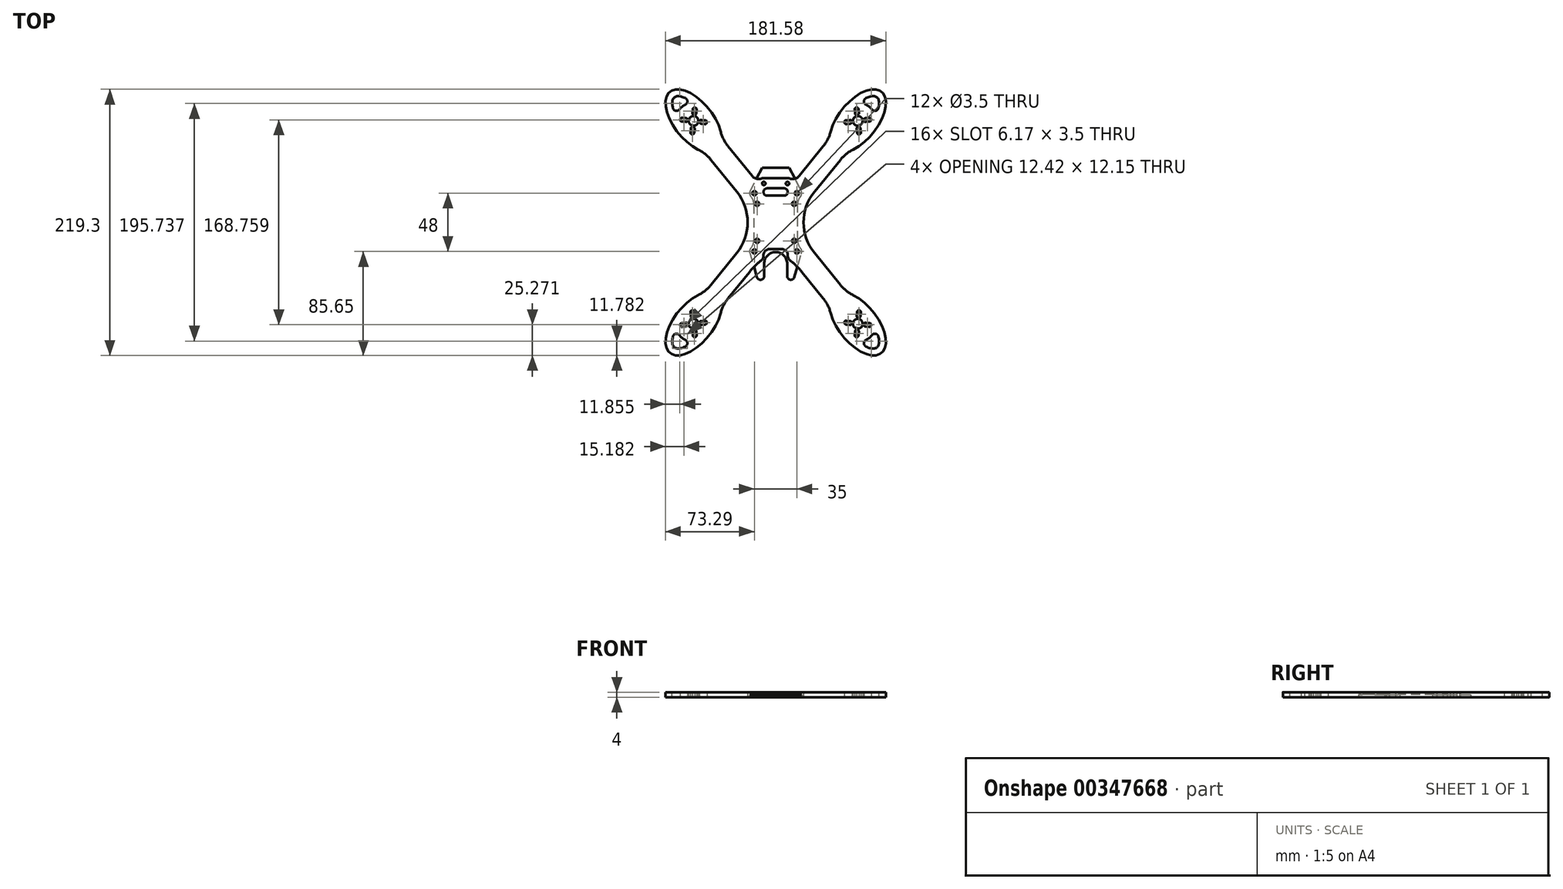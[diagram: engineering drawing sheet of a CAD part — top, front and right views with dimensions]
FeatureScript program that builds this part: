
annotation { "Feature Type Name" : "Feature", "Feature Type Description" : "" }
export const myFeature = defineFeature(function(context is Context, id is Id, definition is map)
    precondition{}
    {
        {
            var Q0;
            Q0=qCreatedBy(makeId("Top.planeOp"),FACE);
            var sketch = newSketch(context, id + "F0", { "sketchPlane" : qUnion([Q0])});
            skCircle(sketch, "E0", {"center": v(0, 0) * mm, "radius": 107.5 * mm, "construction": true});
            skCircle(sketch, "E1", {"center": v(-67.65, 83.54) * mm, "radius": 63.5 * mm, "construction": true});
            skLineSegment(sketch, "E2", {"start": v(-67.65, 83.54) * mm, "end": v(0, 0) * mm, "construction": true});
            skCircle(sketch, "E3", {"center": v(-67.65, 83.54) * mm, "radius": 4 * mm});
            skEllipticalArc(sketch, "E4", {});
            skLineSegment(sketch, "E5", {"start": v(-87.16, 107.63) * mm, "end": v(-67.65, 83.54) * mm, "construction": true});
            skLineSegment(sketch, "E6", {"start": v(-80.09, 73.47) * mm, "end": v(-55.22, 93.61) * mm, "construction": true});
            skLineSegment(sketch, "E7", {"start": v(-53.23, 51.43) * mm, "end": v(-31.97, 25.17) * mm});
            skLineSegment(sketch, "E8", {"start": v(-39.24, 62.76) * mm, "end": v(-21.56, 40.92) * mm});
            skLineSegment(sketch, "E9", {"start": v(-67.65, 83.54) * mm, "end": v(-66.97, 90) * mm, "construction": true});
            skLineSegment(sketch, "E10", {"start": v(-66.97, 90) * mm, "end": v(-66.66, 93) * mm, "construction": true});
            skArc(sketch, "E11.0.startCap", {"start": v(-65.38, 89.84) * mm, "mid": v(-67.14, 88.42) * mm, "end": v(-68.56, 90.17) * mm});
            skArc(sketch, "E11.0.endCap", {"start": v(-68.25, 93.16) * mm, "mid": v(-66.5, 94.58) * mm, "end": v(-65.07, 92.82) * mm});
            skLineSegment(sketch, "E11.0.left", {"start": v(-68.56, 90.17) * mm, "end": v(-68.25, 93.16) * mm});
            skLineSegment(sketch, "E11.0.right", {"start": v(-65.38, 89.84) * mm, "end": v(-65.07, 92.82) * mm});
            skArc(sketch, "E12.1.0", {"start": v(-77.27, 82.94) * mm, "mid": v(-78.7, 84.7) * mm, "end": v(-76.93, 86.13) * mm});
            skLineSegment(sketch, "E12.1.1", {"start": v(-74.28, 82.63) * mm, "end": v(-77.27, 82.94) * mm});
            skArc(sketch, "E12.1.2", {"start": v(-73.95, 85.81) * mm, "mid": v(-72.53, 84.06) * mm, "end": v(-74.28, 82.63) * mm});
            skLineSegment(sketch, "E12.1.3", {"start": v(-73.95, 85.81) * mm, "end": v(-76.93, 86.13) * mm});
            skArc(sketch, "E12.2.0", {"start": v(-67.05, 73.93) * mm, "mid": v(-68.81, 72.5) * mm, "end": v(-70.24, 74.26) * mm});
            skLineSegment(sketch, "E12.2.1", {"start": v(-66.74, 76.91) * mm, "end": v(-67.05, 73.93) * mm});
            skArc(sketch, "E12.2.2", {"start": v(-69.92, 77.25) * mm, "mid": v(-68.16, 78.67) * mm, "end": v(-66.74, 76.91) * mm});
            skLineSegment(sketch, "E12.2.3", {"start": v(-69.92, 77.25) * mm, "end": v(-70.24, 74.26) * mm});
            skArc(sketch, "E12.3.0", {"start": v(-58.04, 84.14) * mm, "mid": v(-56.61, 82.38) * mm, "end": v(-58.37, 80.96) * mm});
            skLineSegment(sketch, "E12.3.1", {"start": v(-61.02, 84.45) * mm, "end": v(-58.04, 84.14) * mm});
            skArc(sketch, "E12.3.2", {"start": v(-61.35, 81.27) * mm, "mid": v(-62.78, 83.03) * mm, "end": v(-61.02, 84.45) * mm});
            skLineSegment(sketch, "E12.3.3", {"start": v(-61.35, 81.27) * mm, "end": v(-58.37, 80.96) * mm});
            skEllipticalArc(sketch, "E13", {});
            skLineSegment(sketch, "E14", {"start": v(-83.38, 102.97) * mm, "end": v(-67.65, 83.54) * mm, "construction": true});
            skArc(sketch, "E15", {"start": v(-79.37, 92.91) * mm, "mid": v(-77.1, 95.2) * mm, "end": v(-74.38, 96.95) * mm});
            skPoint(sketch, "E16.orphan", {"position": v(-81.22, 85.81) * mm});
            skPoint(sketch, "E17.orphan", {"position": v(-67.05, 97.28) * mm});
            skPoint(sketch, "E18.visualSharp", {"position": v(-82.11, 87.53) * mm});
            skArc(sketch, "E18.filletArc", {"start": v(-84.61, 94.04) * mm, "mid": v(-82.34, 91.85) * mm, "end": v(-79.37, 92.91) * mm});
            skPoint(sketch, "E19.visualSharp", {"position": v(-68.55, 98.52) * mm});
            skArc(sketch, "E19.filletArc", {"start": v(-74.38, 96.95) * mm, "mid": v(-72.73, 99.64) * mm, "end": v(-74.4, 102.32) * mm});
            skPoint(sketch, "E20.visualSharp", {"position": v(-58.52, 57.96) * mm});
            skArc(sketch, "E20.filletArc", {"start": v(-53.23, 51.43) * mm, "mid": v(-58.12, 56.29) * mm, "end": v(-63.94, 59.99) * mm});
            skPoint(sketch, "E21.visualSharp", {"position": v(-44.53, 69.29) * mm});
            skArc(sketch, "E21.filletArc", {"start": v(-45.38, 75.01) * mm, "mid": v(-42.98, 68.55) * mm, "end": v(-39.24, 62.76) * mm});
            skArc(sketch, "E22", {"start": v(-23.05, 0) * mm, "mid": v(-25.35, 13.35) * mm, "end": v(-31.97, 25.17) * mm});
            skPoint(sketch, "E23.orphan", {"position": v(0, 14.3) * mm});
            skCircle(sketch, "E24", {"center": v(-15.25, 15.25) * mm, "radius": 1.75 * mm});
            skCircle(sketch, "E25", {"center": v(-17.5, 24) * mm, "radius": 1.75 * mm});
            skLineSegment(sketch, "E26", {"start": v(-23.05, 0) * mm, "end": v(0, 0) * mm, "construction": true});
            skCircle(sketch, "E27.MirrorC", {"center": v(17.5, 24) * mm, "radius": 1.75 * mm});
            skCircle(sketch, "E28.MirrorC", {"center": v(15.25, 15.25) * mm, "radius": 1.75 * mm});
            skArc(sketch, "E29.MirrorCS", {"start": v(23.05, 0) * mm, "mid": v(25.35, 13.35) * mm, "end": v(31.97, 25.17) * mm});
            skLineSegment(sketch, "E30.MirrorCS", {"start": v(53.23, 51.43) * mm, "end": v(31.97, 25.17) * mm});
            skLineSegment(sketch, "E31.MirrorCS", {"start": v(39.24, 62.76) * mm, "end": v(21.56, 40.92) * mm});
            skArc(sketch, "E32.MirrorCS", {"start": v(53.23, 51.43) * mm, "mid": v(58.12, 56.29) * mm, "end": v(63.94, 59.99) * mm});
            skArc(sketch, "E33.MirrorCS", {"start": v(45.38, 75.01) * mm, "mid": v(42.98, 68.55) * mm, "end": v(39.24, 62.76) * mm});
            skEllipticalArc(sketch, "E34.MirrorCS", {});
            skEllipticalArc(sketch, "E35.MirrorCS", {});
            skArc(sketch, "E36.MirrorCS", {"start": v(74.38, 96.95) * mm, "mid": v(72.73, 99.64) * mm, "end": v(74.4, 102.32) * mm});
            skArc(sketch, "E37.MirrorCS", {"start": v(79.37, 92.91) * mm, "mid": v(77.1, 95.2) * mm, "end": v(74.38, 96.95) * mm});
            skArc(sketch, "E38.MirrorCS", {"start": v(84.61, 94.04) * mm, "mid": v(82.34, 91.85) * mm, "end": v(79.37, 92.91) * mm});
            skArc(sketch, "E39.MirrorCS", {"start": v(68.25, 93.16) * mm, "mid": v(66.5, 94.58) * mm, "end": v(65.07, 92.82) * mm});
            skLineSegment(sketch, "E40.MirrorCS", {"start": v(68.56, 90.17) * mm, "end": v(68.25, 93.16) * mm});
            skArc(sketch, "E41.MirrorCS", {"start": v(65.38, 89.84) * mm, "mid": v(67.14, 88.42) * mm, "end": v(68.56, 90.17) * mm});
            skLineSegment(sketch, "E42.MirrorCS", {"start": v(65.38, 89.84) * mm, "end": v(65.07, 92.82) * mm});
            skLineSegment(sketch, "E43.MirrorCS", {"start": v(66.97, 90) * mm, "end": v(66.66, 93) * mm, "construction": true});
            skCircle(sketch, "E44.MirrorC", {"center": v(67.65, 83.54) * mm, "radius": 4 * mm});
            skLineSegment(sketch, "E45.MirrorCS", {"start": v(73.95, 85.81) * mm, "end": v(76.93, 86.13) * mm});
            skArc(sketch, "E46.MirrorCS", {"start": v(77.27, 82.94) * mm, "mid": v(78.7, 84.7) * mm, "end": v(76.93, 86.13) * mm});
            skLineSegment(sketch, "E47.MirrorCS", {"start": v(74.28, 82.63) * mm, "end": v(77.27, 82.94) * mm});
            skArc(sketch, "E48.MirrorCS", {"start": v(73.95, 85.81) * mm, "mid": v(72.53, 84.06) * mm, "end": v(74.28, 82.63) * mm});
            skLineSegment(sketch, "E49.MirrorCS", {"start": v(61.02, 84.45) * mm, "end": v(58.04, 84.14) * mm});
            skArc(sketch, "E50.MirrorCS", {"start": v(61.35, 81.27) * mm, "mid": v(62.78, 83.03) * mm, "end": v(61.02, 84.45) * mm});
            skLineSegment(sketch, "E51.MirrorCS", {"start": v(61.35, 81.27) * mm, "end": v(58.37, 80.96) * mm});
            skArc(sketch, "E52.MirrorCS", {"start": v(58.04, 84.14) * mm, "mid": v(56.61, 82.38) * mm, "end": v(58.37, 80.96) * mm});
            skArc(sketch, "E53.MirrorCS", {"start": v(69.92, 77.25) * mm, "mid": v(68.16, 78.67) * mm, "end": v(66.74, 76.91) * mm});
            skLineSegment(sketch, "E54.MirrorCS", {"start": v(66.74, 76.91) * mm, "end": v(67.05, 73.93) * mm});
            skArc(sketch, "E55.MirrorCS", {"start": v(67.05, 73.93) * mm, "mid": v(68.81, 72.5) * mm, "end": v(70.24, 74.26) * mm});
            skLineSegment(sketch, "E56.MirrorCS", {"start": v(69.92, 77.25) * mm, "end": v(70.24, 74.26) * mm});
            skArc(sketch, "E57.MirrorCS", {"start": v(-23.05, 0) * mm, "mid": v(-25.35, -13.35) * mm, "end": v(-31.97, -25.17) * mm});
            skCircle(sketch, "E58.MirrorC", {"center": v(-15.25, -15.25) * mm, "radius": 1.75 * mm});
            skArc(sketch, "E59.MirrorCS", {"start": v(-21.56, -40.92) * mm, "mid": v(-17, -35.91) * mm, "end": v(-11.92, -31.44) * mm});
            skArc(sketch, "E60.MirrorCS", {"start": v(-10, -27.5) * mm, "mid": v(-10.5, -29.7) * mm, "end": v(-11.92, -31.44) * mm});
            skArc(sketch, "E61.MirrorCS", {"start": v(-10, -27) * mm, "mid": v(-8.54, -23.46) * mm, "end": v(-5, -22) * mm});
            skLineSegment(sketch, "E62.MirrorCS", {"start": v(-5, -22) * mm, "end": v(5, -22) * mm});
            skArc(sketch, "E63.MirrorCS", {"start": v(5, -22) * mm, "mid": v(8.54, -23.46) * mm, "end": v(10, -27) * mm});
            skArc(sketch, "E64.MirrorCS", {"start": v(11.92, -31.44) * mm, "mid": v(10.5, -29.7) * mm, "end": v(10, -27.5) * mm});
            skArc(sketch, "E65.MirrorCS", {"start": v(11.92, -31.44) * mm, "mid": v(17, -35.91) * mm, "end": v(21.56, -40.92) * mm});
            skLineSegment(sketch, "E66.MirrorCS", {"start": v(39.24, -62.76) * mm, "end": v(21.56, -40.92) * mm});
            skLineSegment(sketch, "E67.MirrorCS", {"start": v(-39.24, -62.76) * mm, "end": v(-21.56, -40.92) * mm});
            skArc(sketch, "E68.MirrorCS", {"start": v(23.05, 0) * mm, "mid": v(25.35, -13.35) * mm, "end": v(31.97, -25.17) * mm});
            skLineSegment(sketch, "E69.MirrorCS", {"start": v(53.23, -51.43) * mm, "end": v(31.97, -25.17) * mm});
            skLineSegment(sketch, "E70.MirrorCS", {"start": v(-53.23, -51.43) * mm, "end": v(-31.97, -25.17) * mm});
            skCircle(sketch, "E71.MirrorC", {"center": v(-17.5, -24) * mm, "radius": 1.75 * mm});
            skCircle(sketch, "E72.MirrorC", {"center": v(17.5, -24) * mm, "radius": 1.75 * mm});
            skCircle(sketch, "E73.MirrorC", {"center": v(15.25, -15.25) * mm, "radius": 1.75 * mm});
            skArc(sketch, "E74.MirrorCS", {"start": v(-53.23, -51.43) * mm, "mid": v(-58.12, -56.29) * mm, "end": v(-63.94, -59.99) * mm});
            skArc(sketch, "E75.MirrorCS", {"start": v(-45.38, -75.01) * mm, "mid": v(-42.98, -68.55) * mm, "end": v(-39.24, -62.76) * mm});
            skArc(sketch, "E76.MirrorCS", {"start": v(45.38, -75.01) * mm, "mid": v(42.98, -68.55) * mm, "end": v(39.24, -62.76) * mm});
            skArc(sketch, "E77.MirrorCS", {"start": v(53.23, -51.43) * mm, "mid": v(58.12, -56.29) * mm, "end": v(63.94, -59.99) * mm});
            skEllipticalArc(sketch, "E78.MirrorCS", {});
            skLineSegment(sketch, "E79.MirrorCS", {"start": v(68.56, -90.17) * mm, "end": v(68.25, -93.16) * mm});
            skLineSegment(sketch, "E80.MirrorCS", {"start": v(73.95, -85.81) * mm, "end": v(76.93, -86.13) * mm});
            skEllipticalArc(sketch, "E81.MirrorCS", {});
            skArc(sketch, "E82.MirrorCS", {"start": v(79.37, -92.91) * mm, "mid": v(77.1, -95.2) * mm, "end": v(74.38, -96.95) * mm});
            skArc(sketch, "E83.MirrorCS", {"start": v(84.61, -94.04) * mm, "mid": v(82.34, -91.85) * mm, "end": v(79.37, -92.91) * mm});
            skArc(sketch, "E84.MirrorCS", {"start": v(74.38, -96.95) * mm, "mid": v(72.73, -99.64) * mm, "end": v(74.4, -102.32) * mm});
            skLineSegment(sketch, "E85.MirrorCS", {"start": v(65.38, -89.84) * mm, "end": v(65.07, -92.82) * mm});
            skLineSegment(sketch, "E86.MirrorCS", {"start": v(69.92, -77.25) * mm, "end": v(70.24, -74.26) * mm});
            skLineSegment(sketch, "E87.MirrorCS", {"start": v(61.35, -81.27) * mm, "end": v(58.37, -80.96) * mm});
            skLineSegment(sketch, "E88.MirrorCS", {"start": v(74.28, -82.63) * mm, "end": v(77.27, -82.94) * mm});
            skLineSegment(sketch, "E89.MirrorCS", {"start": v(66.74, -76.91) * mm, "end": v(67.05, -73.93) * mm});
            skLineSegment(sketch, "E90.MirrorCS", {"start": v(61.02, -84.45) * mm, "end": v(58.04, -84.14) * mm});
            skLineSegment(sketch, "E91.MirrorCS", {"start": v(66.97, -90) * mm, "end": v(66.66, -93) * mm, "construction": true});
            skArc(sketch, "E92.MirrorCS", {"start": v(67.05, -73.93) * mm, "mid": v(68.81, -72.5) * mm, "end": v(70.24, -74.26) * mm});
            skArc(sketch, "E93.MirrorCS", {"start": v(61.35, -81.27) * mm, "mid": v(62.78, -83.03) * mm, "end": v(61.02, -84.45) * mm});
            skArc(sketch, "E94.MirrorCS", {"start": v(65.38, -89.84) * mm, "mid": v(67.14, -88.42) * mm, "end": v(68.56, -90.17) * mm});
            skArc(sketch, "E95.MirrorCS", {"start": v(77.27, -82.94) * mm, "mid": v(78.7, -84.7) * mm, "end": v(76.93, -86.13) * mm});
            skArc(sketch, "E96.MirrorCS", {"start": v(69.92, -77.25) * mm, "mid": v(68.16, -78.67) * mm, "end": v(66.74, -76.91) * mm});
            skArc(sketch, "E97.MirrorCS", {"start": v(68.25, -93.16) * mm, "mid": v(66.5, -94.58) * mm, "end": v(65.07, -92.82) * mm});
            skArc(sketch, "E98.MirrorCS", {"start": v(58.04, -84.14) * mm, "mid": v(56.61, -82.38) * mm, "end": v(58.37, -80.96) * mm});
            skArc(sketch, "E99.MirrorCS", {"start": v(73.95, -85.81) * mm, "mid": v(72.53, -84.06) * mm, "end": v(74.28, -82.63) * mm});
            skCircle(sketch, "E100.MirrorC", {"center": v(67.65, -83.54) * mm, "radius": 4 * mm});
            skEllipticalArc(sketch, "E101.MirrorCS", {});
            skEllipticalArc(sketch, "E102.MirrorCS", {});
            skArc(sketch, "E103.MirrorCS", {"start": v(-84.61, -94.04) * mm, "mid": v(-82.34, -91.85) * mm, "end": v(-79.37, -92.91) * mm});
            skArc(sketch, "E104.MirrorCS", {"start": v(-79.37, -92.91) * mm, "mid": v(-77.1, -95.2) * mm, "end": v(-74.38, -96.95) * mm});
            skArc(sketch, "E105.MirrorCS", {"start": v(-74.38, -96.95) * mm, "mid": v(-72.73, -99.64) * mm, "end": v(-74.4, -102.32) * mm});
            skArc(sketch, "E106.MirrorCS", {"start": v(-68.25, -93.16) * mm, "mid": v(-66.5, -94.58) * mm, "end": v(-65.07, -92.82) * mm});
            skLineSegment(sketch, "E107.MirrorCS", {"start": v(-65.38, -89.84) * mm, "end": v(-65.07, -92.82) * mm});
            skArc(sketch, "E108.MirrorCS", {"start": v(-65.38, -89.84) * mm, "mid": v(-67.14, -88.42) * mm, "end": v(-68.56, -90.17) * mm});
            skLineSegment(sketch, "E109.MirrorCS", {"start": v(-68.56, -90.17) * mm, "end": v(-68.25, -93.16) * mm});
            skLineSegment(sketch, "E110.MirrorCS", {"start": v(-66.97, -90) * mm, "end": v(-66.66, -93) * mm, "construction": true});
            skLineSegment(sketch, "E111.MirrorCS", {"start": v(-73.95, -85.81) * mm, "end": v(-76.93, -86.13) * mm});
            skArc(sketch, "E112.MirrorCS", {"start": v(-77.27, -82.94) * mm, "mid": v(-78.7, -84.7) * mm, "end": v(-76.93, -86.13) * mm});
            skLineSegment(sketch, "E113.MirrorCS", {"start": v(-74.28, -82.63) * mm, "end": v(-77.27, -82.94) * mm});
            skArc(sketch, "E114.MirrorCS", {"start": v(-73.95, -85.81) * mm, "mid": v(-72.53, -84.06) * mm, "end": v(-74.28, -82.63) * mm});
            skCircle(sketch, "E115.MirrorC", {"center": v(-67.65, -83.54) * mm, "radius": 4 * mm});
            skLineSegment(sketch, "E116.MirrorCS", {"start": v(-61.02, -84.45) * mm, "end": v(-58.04, -84.14) * mm});
            skArc(sketch, "E117.MirrorCS", {"start": v(-58.04, -84.14) * mm, "mid": v(-56.61, -82.38) * mm, "end": v(-58.37, -80.96) * mm});
            skLineSegment(sketch, "E118.MirrorCS", {"start": v(-61.35, -81.27) * mm, "end": v(-58.37, -80.96) * mm});
            skArc(sketch, "E119.MirrorCS", {"start": v(-61.35, -81.27) * mm, "mid": v(-62.78, -83.03) * mm, "end": v(-61.02, -84.45) * mm});
            skArc(sketch, "E120.MirrorCS", {"start": v(-69.92, -77.25) * mm, "mid": v(-68.16, -78.67) * mm, "end": v(-66.74, -76.91) * mm});
            skLineSegment(sketch, "E121.MirrorCS", {"start": v(-66.74, -76.91) * mm, "end": v(-67.05, -73.93) * mm});
            skArc(sketch, "E122.MirrorCS", {"start": v(-67.05, -73.93) * mm, "mid": v(-68.81, -72.5) * mm, "end": v(-70.24, -74.26) * mm});
            skLineSegment(sketch, "E123.MirrorCS", {"start": v(-69.92, -77.25) * mm, "end": v(-70.24, -74.26) * mm});
            skLineSegment(sketch, "E124", {"start": v(-10, -27) * mm, "end": v(-10, -27.5) * mm});
            skLineSegment(sketch, "E125", {"start": v(10, -27) * mm, "end": v(10, -27.5) * mm});
            skCircle(sketch, "E126", {"center": v(-9.75, 32) * mm, "radius": 1.4 * mm});
            skCircle(sketch, "E127", {"center": v(9.75, 32) * mm, "radius": 1.4 * mm});
            skArc(sketch, "E128", {"start": v(-9.75, 36.5) * mm, "mid": v(-10.6, 36.42) * mm, "end": v(-11.4, 36.18) * mm});
            skArc(sketch, "E129", {"start": v(11.4, 36.18) * mm, "mid": v(10.6, 36.42) * mm, "end": v(9.75, 36.5) * mm});
            skLineSegment(sketch, "E130", {"start": v(-21.56, 40.92) * mm, "end": v(-19.42, 38.29) * mm});
            skLineSegment(sketch, "E131", {"start": v(21.56, 40.92) * mm, "end": v(19.42, 38.29) * mm});
            skArc(sketch, "E132", {"start": v(-19.42, 38.29) * mm, "mid": v(-15.76, 35.92) * mm, "end": v(-11.4, 36.18) * mm});
            skArc(sketch, "E133", {"start": v(11.4, 36.18) * mm, "mid": v(15.76, 35.92) * mm, "end": v(19.42, 38.29) * mm});
            skLineSegment(sketch, "E134", {"start": v(-9.75, 36.5) * mm, "end": v(9.75, 36.5) * mm});
            skLineSegment(sketch, "E135.bottom", {"start": v(-7, 28) * mm, "end": v(7, 28) * mm});
            skLineSegment(sketch, "E135.top", {"start": v(-7, 22) * mm, "end": v(7, 22) * mm});
            skLineSegment(sketch, "E135.left", {"start": v(-10, 25) * mm, "end": v(-10, 25) * mm});
            skLineSegment(sketch, "E135.right", {"start": v(10, 25) * mm, "end": v(10, 25) * mm});
            skPoint(sketch, "E136.visualSharp", {"position": v(-10, 28) * mm});
            skArc(sketch, "E136.filletArc", {"start": v(-7, 28) * mm, "mid": v(-9.12, 27.12) * mm, "end": v(-10, 25) * mm});
            skPoint(sketch, "E137.visualSharp", {"position": v(-10, 22) * mm});
            skArc(sketch, "E137.filletArc", {"start": v(-10, 25) * mm, "mid": v(-9.12, 22.88) * mm, "end": v(-7, 22) * mm});
            skPoint(sketch, "E138.visualSharp", {"position": v(10, 22) * mm});
            skArc(sketch, "E138.filletArc", {"start": v(7, 22) * mm, "mid": v(9.12, 22.88) * mm, "end": v(10, 25) * mm});
            skPoint(sketch, "E139.visualSharp", {"position": v(10, 28) * mm});
            skArc(sketch, "E139.filletArc", {"start": v(10, 25) * mm, "mid": v(9.12, 27.12) * mm, "end": v(7, 28) * mm});
            const initialGuessF0  = {"E4": [-0.06765194203785749, 0.0835431908566244, 0.6293203910498372, -0.7771459614569712, 0.031, 0.016, 0.8420594111853004, 5.441125895994282], "E13": [-0.06765194203785749, 0.0835431908566244, -0.6293203910498373, 0.7771459614569711, 0.025, 0.01, 5.565504361891691, 0.7176809452878963], "E34.MirrorCS": [0.06765194203785746, 0.08354319085662443, -0.6293203910498371, -0.7771459614569712, 0.031, 0.016, 0.842059411185305, 5.441125895994286], "E35.MirrorCS": [0.06765194203785747, 0.08354319085662441, 0.6293203910498371, 0.7771459614569712, 0.025, 0.01, 5.565504361891689, 0.7176809452878956], "E78.MirrorCS": [0.06765194203785746, -0.08354319085662443, -0.6293203910498371, 0.7771459614569712, 0.031, 0.016, 0.8420594111852998, 5.441125895994281], "E81.MirrorCS": [0.06765194203785747, -0.08354319085662441, 0.6293203910498371, -0.7771459614569712, 0.025, 0.01, 5.565504361891691, 0.717680945287897], "E101.MirrorCS": [-0.06765194203785749, -0.0835431908566244, 0.6293203910498372, 0.7771459614569712, 0.031, 0.016, 0.8420594111853045, 5.441125895994286], "E102.MirrorCS": [-0.06765194203785749, -0.0835431908566244, -0.6293203910498373, -0.7771459614569711, 0.025, 0.01, 5.56550436189169, 0.7176809452878958]};
            skSetInitialGuess(sketch, initialGuessF0);
            skSolve(sketch);
        }
        {
            var Q0;
            Q0=qSketchRegion(id+"F0",true);
            extrude(context, id + "F1", {"entities" : qUnion([Q0]), "depth" : 4 * mm});
        }
        {
            var Q0;
            Q0=qCreatedBy(makeId("Top.planeOp"),FACE);
            var sketch = newSketch(context, id + "F2", { "sketchPlane" : qUnion([Q0])});
            skLineSegment(sketch, "E140.bottom", {"start": v(-17.5, 28) * mm, "end": v(0, 28) * mm});
            skLineSegment(sketch, "E140.left", {"start": v(-18, 14.74) * mm, "end": v(-18, 0) * mm});
            skArc(sketch, "E141", {"start": v(-17.5, 28) * mm, "mid": v(-21.15, 25.65) * mm, "end": v(-20.5, 21.35) * mm});
            skLineSegment(sketch, "E142", {"start": v(-50, 0) * mm, "end": v(50, 0) * mm, "construction": true});
            skLineSegment(sketch, "E143", {"start": v(0, 50) * mm, "end": v(0, -50) * mm, "construction": true});
            skPoint(sketch, "E144.visualSharp", {"position": v(-18, 20.03) * mm});
            skArc(sketch, "E144.filletArc", {"start": v(-18, 14.74) * mm, "mid": v(-18.65, 18.28) * mm, "end": v(-20.5, 21.35) * mm});
            skLineSegment(sketch, "E145.MirrorCS", {"start": v(17.5, 28) * mm, "end": v(0, 28) * mm});
            skArc(sketch, "E146.MirrorCS", {"start": v(17.5, 28) * mm, "mid": v(21.15, 25.65) * mm, "end": v(20.5, 21.35) * mm});
            skArc(sketch, "E147.MirrorCS", {"start": v(18, 14.74) * mm, "mid": v(18.65, 18.28) * mm, "end": v(20.5, 21.35) * mm});
            skLineSegment(sketch, "E148.MirrorCS", {"start": v(18, 14.74) * mm, "end": v(18, 0) * mm});
            skLineSegment(sketch, "E149.MirrorCS", {"start": v(-18, -14.74) * mm, "end": v(-18, 0) * mm});
            skArc(sketch, "E150.MirrorCS", {"start": v(-18, -14.74) * mm, "mid": v(-18.65, -18.28) * mm, "end": v(-20.5, -21.35) * mm});
            skArc(sketch, "E151.MirrorCS", {"start": v(-21.33, -25.14) * mm, "mid": v(-21.4, -23.14) * mm, "end": v(-20.5, -21.35) * mm});
            skArc(sketch, "E152.MirrorCS", {"start": v(21.33, -25.14) * mm, "mid": v(21.4, -23.14) * mm, "end": v(20.5, -21.35) * mm});
            skArc(sketch, "E153.MirrorCS", {"start": v(18, -14.74) * mm, "mid": v(18.65, -18.28) * mm, "end": v(20.5, -21.35) * mm});
            skLineSegment(sketch, "E154.MirrorCS", {"start": v(18, -14.74) * mm, "end": v(18, 0) * mm});
            skArc(sketch, "E155", {"start": v(9.5, -34) * mm, "mid": v(0, -24.5) * mm, "end": v(-9.5, -34) * mm});
            skLineSegment(sketch, "E156", {"start": v(-9.5, -34) * mm, "end": v(-9.5, -44.35) * mm});
            skLineSegment(sketch, "E157", {"start": v(9.5, -34) * mm, "end": v(9.5, -44.35) * mm});
            skLineSegment(sketch, "E158", {"start": v(-21.33, -25.14) * mm, "end": v(-15.38, -45.2) * mm});
            skLineSegment(sketch, "E159", {"start": v(15.38, -45.2) * mm, "end": v(21.33, -25.14) * mm});
            skPoint(sketch, "E160.orphan", {"position": v(-17.5, -28) * mm});
            skPoint(sketch, "E161.orphan", {"position": v(17.5, -28) * mm});
            skPoint(sketch, "E162.visualSharp", {"position": v(-9.5, -65) * mm});
            skArc(sketch, "E162.filletArc", {"start": v(-15.38, -45.2) * mm, "mid": v(-12.07, -47.32) * mm, "end": v(-9.5, -44.35) * mm});
            skPoint(sketch, "E163.visualSharp", {"position": v(9.5, -65) * mm});
            skArc(sketch, "E163.filletArc", {"start": v(9.5, -44.35) * mm, "mid": v(12.07, -47.32) * mm, "end": v(15.38, -45.2) * mm});
            skCircle(sketch, "E164", {"center": v(-17.5, -24) * mm, "radius": 1.75 * mm});
            skCircle(sketch, "E165.MirrorC", {"center": v(17.5, -24) * mm, "radius": 1.75 * mm});
            skCircle(sketch, "E166.MirrorC", {"center": v(-17.5, 24) * mm, "radius": 1.75 * mm});
            skCircle(sketch, "E167.MirrorC", {"center": v(17.5, 24) * mm, "radius": 1.75 * mm});
            skLineSegment(sketch, "E168", {"start": v(-21.04, 25.86) * mm, "end": v(-11, 45) * mm});
            skLineSegment(sketch, "E169", {"start": v(-11, 45) * mm, "end": v(11, 45) * mm});
            skLineSegment(sketch, "E170", {"start": v(11, 45) * mm, "end": v(21.04, 25.86) * mm});
            skSolve(sketch);
        }
        {
            var Q0;
            Q0=makeQuery(id+"F2.imprint","IMPRINT",FACE,{"disambiguationData":[TD([[makeQuery(id+"F2.imprint","IMPRINT",EDGE,{"derivedFrom":sQuery(id+"F2.wireOp",EDGE,"E140.bottom")}),-1.0]])]});
            var Q1;
            {var subQ4=sQuery(id+"F2.wireOp",EDGE,"E140.bottom");Q1=makeQuery(id+"F2.imprint","IMPRINT",FACE,{"disambiguationData":[TD([[makeQuery(id+"F2.imprint","IMPRINT",EDGE,{"derivedFrom":subQ4}),1.0]])]});}
            extrude(context, id + "F3", {"entities" : qUnion([Q0, Q1]), "depth" : 2 * mm});
        }
    });
